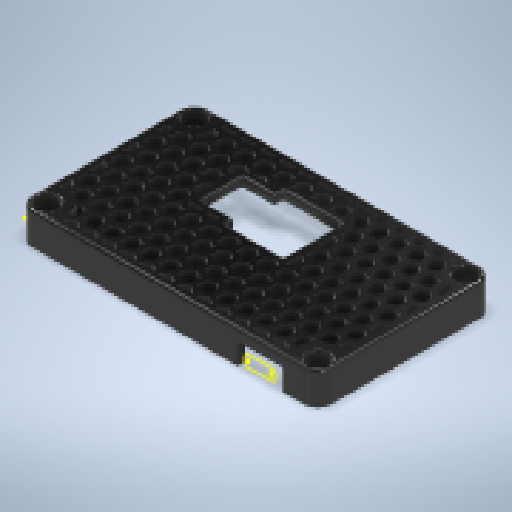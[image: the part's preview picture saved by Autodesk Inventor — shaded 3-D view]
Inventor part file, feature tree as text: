
AUTODESK INVENTOR PART (.ipt)
format: ipt  version: 2025 (Build 290162000, 162)  size: 3,560,448 bytes
history: native  units: mm
features: reference x16, sketch x8, extrude x8, other x5, fillet x4, thicken_offset x4, chamfer x2, projected_geometry x2
ambient origin geometry x8: Origin, YZ Plane, XZ Plane, XY Plane, X Axis, Y Axis, Z Axis, Center Point
bodies: Solid1 (feature_tree)
feature tree (49):
  sketch  "Sketch1"  dims[d0=2.0mm d1=80.0mm]
  extrude  "Extrusion1"  Depth=80.0mm
  extrude  "Extrusion2"  Depth=1.0mm TaperAngle=0.0deg
  extrude  "Extrusion3"  Depth=45.5mm
  fillet  "Fillet2"  Radius=3.2mm
  fillet  "Fillet3"  Radius=6.0mm
  extrude  "Extrusion4"  Depth=1.0mm
  thicken_offset  "Thicken1"
  thicken_offset  "Thicken2"
  thicken_offset  "Thicken3"
  thicken_offset  "Thicken4"
  chamfer  "Chamfer2"  Distance=0.5mm
  chamfer  "Chamfer3"  Distance=1.0mm
  fillet  "Fillet5"  Radius=0.5mm
  extrude  "Extrusion5"  Depth=0.5mm
  fillet  "Fillet6"  Radius=0.5mm
  sketch  "Sketch4"  dims[d14=3.0mm d15=0.0mm d16=1.0mm]
  extrude  "Extrusion7"  Depth=0.5mm
  extrude  "Extrusion8"  Depth=0.5mm TaperAngle=45.0deg
  sketch  "Sketch5"  dims[d22=0.5mm]
  extrude  "Extrusion9"  Depth=0.5mm TaperAngle=45.0deg
  sketch  "Sketch3"  dims[d3=2.0mm d4=1.0mm d5=0.0mm]
  reference  "Reference1"
  reference  "Reference2"
  reference  "Reference3"
  reference  "Reference4"
  reference  "Reference5"
  reference  "Reference6"
  reference  "Reference7"
  projected_geometry  "Projected Loop1"
  projected_geometry  "Projected Loop2"
  sketch  "Sketch Rectangular Pattern3"  dims[d6=6.0mm d7=0.0mm d10=45.5mm d11=3.2mm d13=6.0mm]
  sketch  "Sketch Rectangular Pattern4"  dims[d17=0.5mm]
  sketch  "Sketch Rectangular Pattern5"  dims[d23=0.5mm]
  reference  "Reference8"
  reference  "Reference9"
  reference  "Reference10"
  reference  "Reference11"
  reference  "Reference12"
  reference  "Reference13"
  reference  "Reference14"
  reference  "Reference15"
  reference  "Reference16"
  sketch  "Sketch6"  dims[d24=0.5mm d25=0.5mm d26=1.0mm d27=0.0mm d28=0.5mm d29=0.5mm d30=0.5mm d31=0.5mm d32=2.0mm d33=2.0mm d34=45.0deg d35=1.0mm d36=2.0mm d37=45.0deg d38=1.0mm d39=1.0mm d40=1.0mm d41=2.0mm d42=0.0mm d43=0.0mm d44=0.5mm d46=1.0mm d47=4.0mm d51=0.5mm d53=4.0mm d54=0.5mm d74=60.0mm d76=5.333333mm d77=10.0mm d79=5.333333mm d81=60.0mm d83=5.333333mm d84=10.0mm d86=10.0mm d88=170.0mm d90=5.333333mm d91=10.0mm d93=10.0mm d95=0.0mm d96=0.0mm d100=10.0mm d101=0.0mm d102=12.5mm d103=6.5mm d104=0.5mm d105=2.0mm d106=0.0mm d18=0.5mm d19=0.872665mm d20=0.5mm d21=0.872665mm d97=0.0mm d98=0.0mm d99=0.0mm]
  parser-record x1  (decoder bookkeeping rows leaked as tree rows — omitted from the tree; the rows remain in map.json)
  other  "RemoteCameraModule.iam"
  other  "HEATSINK14x14:1"
  other  "HEATSINK9x9:1"
  other  "OPiZ2W_:1"
note: 1 file-system path scrubbed to <path> (originals preserved in map.json)
